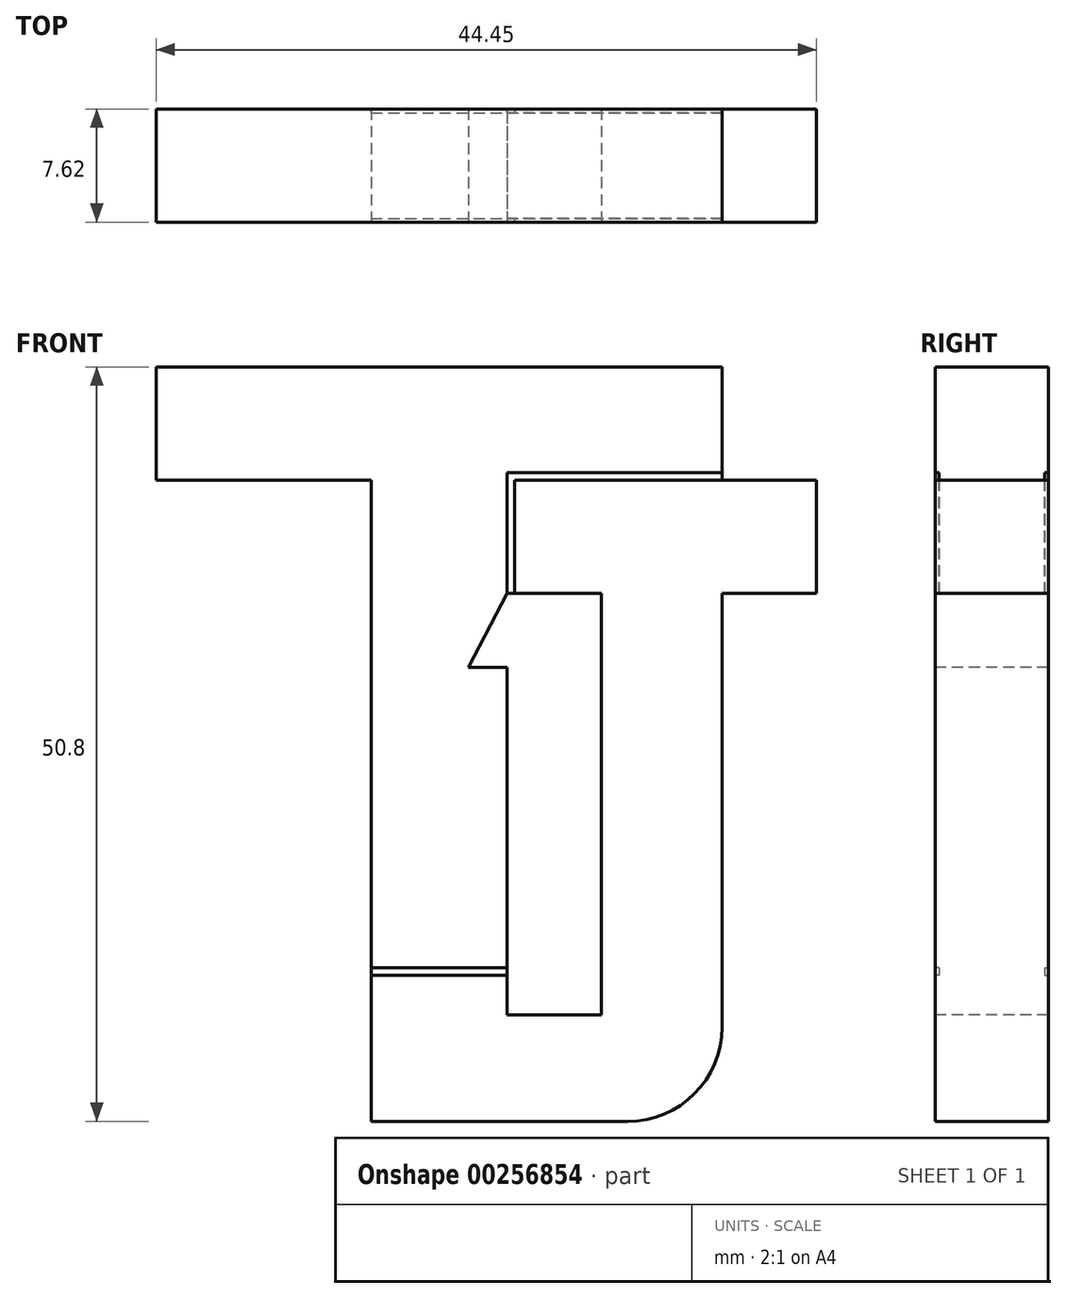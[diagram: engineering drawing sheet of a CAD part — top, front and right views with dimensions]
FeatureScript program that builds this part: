
annotation { "Feature Type Name" : "Feature", "Feature Type Description" : "" }
export const myFeature = defineFeature(function(context is Context, id is Id, definition is map)
    precondition{}
    {
        {
            var Q0;
            Q0=qCreatedBy(makeId("Front.planeOp"),FACE);
            var sketch = newSketch(context, id + "F0", { "sketchPlane" : qUnion([Q0])});
            skLineSegment(sketch, "E0", {"start": v(-48.8, 33.08) * mm, "end": v(-10.7, 33.08) * mm});
            skLineSegment(sketch, "E1", {"start": v(-10.7, 25.46) * mm, "end": v(-25.17, 25.46) * mm});
            skLineSegment(sketch, "E2", {"start": v(-48.8, 33.08) * mm, "end": v(-48.8, 25.46) * mm});
            skLineSegment(sketch, "E3", {"start": v(-48.8, 25.46) * mm, "end": v(-34.32, 25.46) * mm});
            skLineSegment(sketch, "E4", {"start": v(-34.32, 25.46) * mm, "end": v(-34.32, -7.37) * mm});
            skLineSegment(sketch, "E5", {"start": v(-34.32, -7.37) * mm, "end": v(-25.17, -7.37) * mm});
            skLineSegment(sketch, "E6", {"start": v(-25.17, -7.37) * mm, "end": v(-25.17, 12.86) * mm});
            skLineSegment(sketch, "E7", {"start": v(-10.7, 25.46) * mm, "end": v(-4.34, 25.46) * mm});
            skLineSegment(sketch, "E8", {"start": v(-4.34, 25.46) * mm, "end": v(-4.34, 17.84) * mm});
            skLineSegment(sketch, "E9", {"start": v(-4.34, 17.84) * mm, "end": v(-10.7, 17.84) * mm});
            skLineSegment(sketch, "E10", {"start": v(-10.7, 17.84) * mm, "end": v(-10.7, -11.37) * mm});
            skLineSegment(sketch, "E11", {"start": v(-34.32, -7.37) * mm, "end": v(-34.32, -17.72) * mm});
            skLineSegment(sketch, "E12", {"start": v(-34.32, -17.72) * mm, "end": v(-17.04, -17.72) * mm});
            skLineSegment(sketch, "E13", {"start": v(-25.17, -7.37) * mm, "end": v(-25.17, -10.54) * mm});
            skLineSegment(sketch, "E14", {"start": v(-25.17, -10.54) * mm, "end": v(-18.82, -10.54) * mm});
            skLineSegment(sketch, "E15", {"start": v(-18.82, -10.54) * mm, "end": v(-18.82, 17.84) * mm});
            skLineSegment(sketch, "E16", {"start": v(-18.82, 17.84) * mm, "end": v(-25.17, 17.84) * mm});
            skPoint(sketch, "E17.visualSharp", {"position": v(-10.7, -17.72) * mm});
            skArc(sketch, "E17.filletArc", {"start": v(-17.04, -17.72) * mm, "mid": v(-12.55, -15.86) * mm, "end": v(-10.7, -11.37) * mm});
            skLineSegment(sketch, "E18", {"start": v(-25.17, 17.84) * mm, "end": v(-27.76, 12.86) * mm});
            skLineSegment(sketch, "E19", {"start": v(-27.76, 12.86) * mm, "end": v(-25.17, 12.86) * mm});
            skLineSegment(sketch, "E20.trimOffspring", {"start": v(-25.17, 17.84) * mm, "end": v(-25.17, 25.46) * mm});
            skLineSegment(sketch, "E21", {"start": v(-25.17, 25.96) * mm, "end": v(-10.7, 25.96) * mm});
            skLineSegment(sketch, "E22", {"start": v(-25.17, 25.14) * mm, "end": v(-25.17, 25.96) * mm});
            skLineSegment(sketch, "E23", {"start": v(-10.7, 33.08) * mm, "end": v(-10.7, 25.96) * mm});
            skLineSegment(sketch, "E24", {"start": v(-10.7, 25.96) * mm, "end": v(-10.7, 25.46) * mm});
            skLineSegment(sketch, "E25", {"start": v(-24.66, 25.46) * mm, "end": v(-24.66, 17.84) * mm});
            skLineSegment(sketch, "E26", {"start": v(-25.17, -7.88) * mm, "end": v(-34.32, -7.88) * mm});
            skSolve(sketch);
        }
        {
            var Q0;
            Q0=makeQuery(id+"F0.imprint","IMPRINT",FACE,{"disambiguationData":[TD([[makeQuery(id+"F0.imprint","IMPRINT",EDGE,{"derivedFrom":sQuery(id+"F0.wireOp",EDGE,"E0")}),-1.0]])]});
            var Q1;
            Q1=makeQuery(id+"F0.imprint","IMPRINT",FACE,{"disambiguationData":[TD([[makeQuery(id+"F0.imprint","IMPRINT",EDGE,{"derivedFrom":sQuery(id+"F0.wireOp",EDGE,"E5")}),-1.0]])]});
            var Q2;
            {var subQ6=sQuery(id+"F0.wireOp",EDGE,"E7");Q2=makeQuery(id+"F0.imprint","IMPRINT",FACE,{"disambiguationData":[TD([[makeQuery(id+"F0.imprint","IMPRINT",EDGE,{"derivedFrom":subQ6}),-1.0]])]});}
            extrude(context, id + "F1", {"entities" : qUnion([Q0, Q1, Q2]), "oppositeDirection" : true, "depth" : 7.62 * mm});
        }
        {
            var Q0;
            {var subQ0=sQuery(id+"F0.wireOp",EDGE,"E1");Q0=makeQuery(id+"F0.imprint","IMPRINT",FACE,{"disambiguationData":[TD([[makeQuery(id+"F0.imprint","IMPRINT",EDGE,{"derivedFrom":subQ0}),-1.0]])]});}
            var Q1;
            {var subQ3=sQuery(id+"F0.wireOp",EDGE,"E20.trimOffspring");Q1=makeQuery(id+"F0.imprint","IMPRINT",FACE,{"disambiguationData":[TD([[makeQuery(id+"F0.imprint","IMPRINT",EDGE,{"derivedFrom":subQ3}),-1.0]])]});}
            var Q2;
            {var subQ0=sQuery(id+"F0.wireOp",EDGE,"E5");Q2=makeQuery(id+"F0.imprint","IMPRINT",FACE,{"disambiguationData":[TD([[makeQuery(id+"F0.imprint","IMPRINT",EDGE,{"derivedFrom":subQ0}),-1.0]])]});}
            extrude(context, id + "F2", {"entities" : qUnion([Q0, Q1, Q2]), "operationType" : NewBodyOperationType.ADD, "oppositeDirection" : true, "depth" : 7.37 * mm});
        }
        {
            var Q0;
            {var subQ3=sQuery(id+"F0.wireOp",EDGE,"E20.trimOffspring");Q0=makeQuery(id+"F0.imprint","IMPRINT",FACE,{"disambiguationData":[TD([[makeQuery(id+"F0.imprint","IMPRINT",EDGE,{"derivedFrom":subQ3}),-1.0]])]});}
            var Q1;
            {var subQ3=sQuery(id+"F0.wireOp",EDGE,"E21");Q1=makeQuery(id+"F0.imprint","IMPRINT",FACE,{"disambiguationData":[TD([[makeQuery(id+"F0.imprint","IMPRINT",EDGE,{"derivedFrom":subQ3}),-1.0]])]});}
            var Q2;
            {var subQ0=sQuery(id+"F0.wireOp",EDGE,"E5");Q2=makeQuery(id+"F0.imprint","IMPRINT",FACE,{"disambiguationData":[TD([[makeQuery(id+"F0.imprint","IMPRINT",EDGE,{"derivedFrom":subQ0}),-1.0]])]});}
            extrude(context, id + "F3", {"entities" : qUnion([Q0, Q1, Q2]), "operationType" : NewBodyOperationType.REMOVE, "oppositeDirection" : true, "depth" : 0.25 * mm});
        }
        {
            var Q0;
            Q0=makeQuery(id+"F1.opExtrude","CAP_FACE",FACE,{"disambiguationData":[OSD([sQuery(id+"F0.wireOp",EDGE,"E0"),sQuery(id+"F0.wireOp",EDGE,"E1"),sQuery(id+"F0.wireOp",EDGE,"E2"),sQuery(id+"F0.wireOp",EDGE,"E3"),sQuery(id+"F0.wireOp",EDGE,"E4"),sQuery(id+"F0.wireOp",EDGE,"E6"),sQuery(id+"F0.wireOp",EDGE,"E7"),sQuery(id+"F0.wireOp",EDGE,"E8"),sQuery(id+"F0.wireOp",EDGE,"E9"),sQuery(id+"F0.wireOp",EDGE,"E10"),sQuery(id+"F0.wireOp",EDGE,"E11"),sQuery(id+"F0.wireOp",EDGE,"E12"),sQuery(id+"F0.wireOp",EDGE,"E13"),sQuery(id+"F0.wireOp",EDGE,"E14"),sQuery(id+"F0.wireOp",EDGE,"E15"),sQuery(id+"F0.wireOp",EDGE,"E16"),sQuery(id+"F0.wireOp",EDGE,"E17.filletArc"),sQuery(id+"F0.wireOp",EDGE,"E18"),sQuery(id+"F0.wireOp",EDGE,"E19"),sQuery(id+"F0.wireOp",EDGE,"E20.trimOffspring"),sQuery(id+"F0.wireOp",EDGE,"E21"),sQuery(id+"F0.wireOp",EDGE,"E22"),sQuery(id+"F0.wireOp",EDGE,"E23"),sQuery(id+"F0.wireOp",EDGE,"E25")])],"isStart":false});
            var sketch = newSketch(context, id + "F4", { "sketchPlane" : qUnion([Q0])});
            skLineSegment(sketch, "E27", {"start": v(34.32, -7.88) * mm, "end": v(25.17, -7.88) * mm});
            skLineSegment(sketch, "E28", {"start": v(25.17, -7.88) * mm, "end": v(25.17, -7.37) * mm});
            skLineSegment(sketch, "E29", {"start": v(25.17, -7.37) * mm, "end": v(34.32, -7.37) * mm});
            skLineSegment(sketch, "E30", {"start": v(34.32, -7.37) * mm, "end": v(34.32, -7.88) * mm});
            skSolve(sketch);
        }
        {
            var Q0;
            Q0=makeQuery(id+"F4.imprint","IMPRINT",FACE,{"disambiguationData":[TD([[makeQuery(id+"F4.imprint","IMPRINT",EDGE,{"derivedFrom":sQuery(id+"F4.wireOp",EDGE,"E27")}),-1.0]])]});
            extrude(context, id + "F5", {"entities" : qUnion([Q0]), "operationType" : NewBodyOperationType.REMOVE, "oppositeDirection" : true, "depth" : 0.25 * mm});
        }
    });
